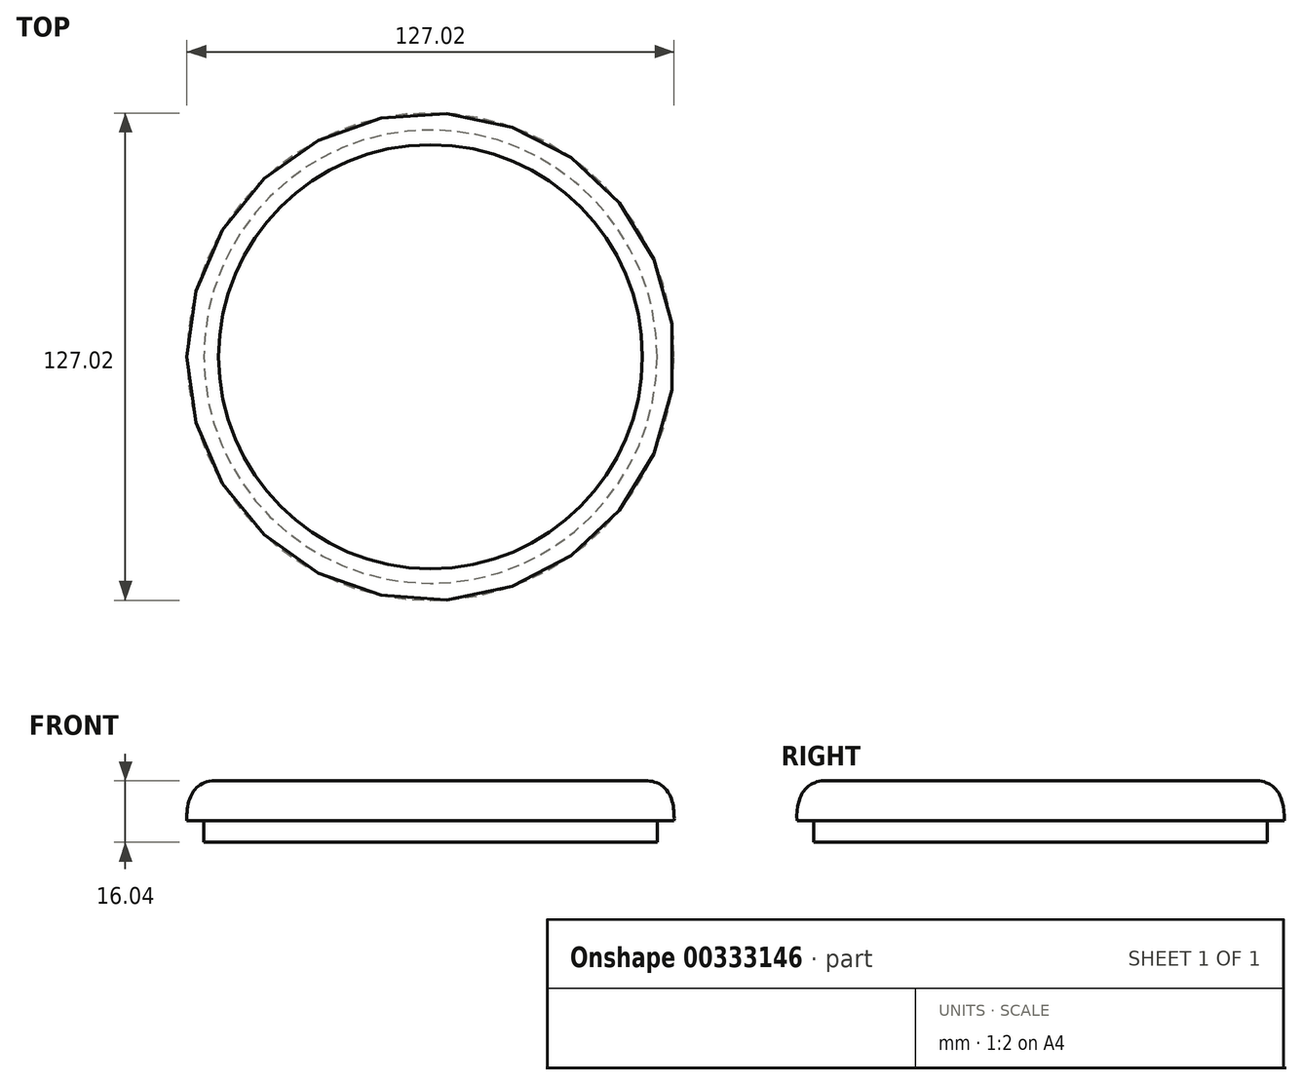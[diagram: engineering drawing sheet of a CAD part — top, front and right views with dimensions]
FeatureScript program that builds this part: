
annotation { "Feature Type Name" : "Feature", "Feature Type Description" : "" }
export const myFeature = defineFeature(function(context is Context, id is Id, definition is map)
    precondition{}
    {
        {
            var Q0;
            Q0=qCreatedBy(makeId("Front.planeOp"),FACE);
            var sketch = newSketch(context, id + "F0", { "sketchPlane" : qUnion([Q0])});
            skLineSegment(sketch, "E0", {"start": v(0, 0) * mm, "end": v(0, 46.52) * mm, "construction": true});
            skLineSegment(sketch, "E1.bottom", {"start": v(0, 0) * mm, "end": v(59.08, 0) * mm});
            skLineSegment(sketch, "E1.top", {"start": v(0, 16.02) * mm, "end": v(55.25, 16.02) * mm});
            skLineSegment(sketch, "E1.left", {"start": v(0, 0) * mm, "end": v(0, 16.02) * mm});
            skFitSpline(sketch, "E2", {"points": [v(63.5, 5.63) * mm, v(61.8, 13.2) * mm, v(55.25, 16.02) * mm], "startDerivative": vector(0.6, 18.9) * mm, "endDerivative": vector(-20.75, -1.08) * mm});
            skLineSegment(sketch, "E3", {"start": v(63.5, 5.63) * mm, "end": v(59.08, 5.63) * mm});
            skLineSegment(sketch, "E4", {"start": v(59.08, 5.63) * mm, "end": v(59.08, 0) * mm});
            skPoint(sketch, "E5.orphan", {"position": v(63.5, 0) * mm});
            skSolve(sketch);
        }
        {
            var Q0;
            Q0 = qSketchRegion(id + "F0", true);
            var Q1;
            Q1=sQuery(id+"F0.wireOp",EDGE,"E1.left");
            revolve(context, id + "F1", {"entities" : qUnion([Q0]), "axis" : qUnion([Q1]), "revolveType" : RevolveType.FULL});
        }
    });
